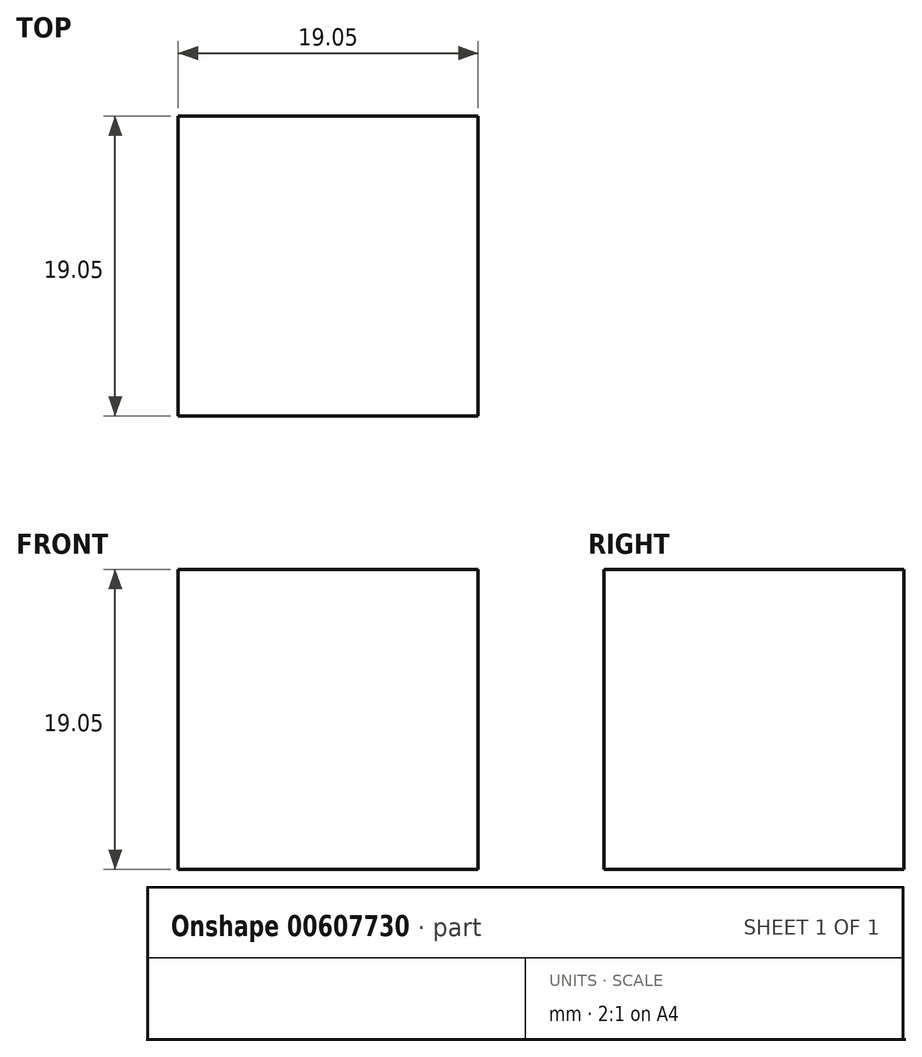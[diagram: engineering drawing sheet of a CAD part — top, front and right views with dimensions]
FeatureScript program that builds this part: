
annotation { "Feature Type Name" : "Feature", "Feature Type Description" : "" }
export const myFeature = defineFeature(function(context is Context, id is Id, definition is map)
    precondition{}
    {
        {
            var Q0;
            Q0=qCreatedBy(makeId("Top.planeOp"),FACE);
            var sketch = newSketch(context, id + "F0", { "sketchPlane" : qUnion([Q0])});
            skLineSegment(sketch, "E0.bottom", {"start": v(-53.08, 12.99) * mm, "end": v(-34.03, 12.99) * mm});
            skLineSegment(sketch, "E0.top", {"start": v(-53.08, 32.04) * mm, "end": v(-34.03, 32.04) * mm});
            skLineSegment(sketch, "E0.left", {"start": v(-53.08, 12.99) * mm, "end": v(-53.08, 32.04) * mm});
            skLineSegment(sketch, "E0.right", {"start": v(-34.03, 12.99) * mm, "end": v(-34.03, 32.04) * mm});
            skSolve(sketch);
        }
        {
            var Q0;
            Q0 = qSketchRegion(id + "F0", true);
            extrude(context, id + "F1", {"entities" : qUnion([Q0]), "depth" : 19.05 * mm, "offsetDistance" : 25.4 * mm});
        }
    });
